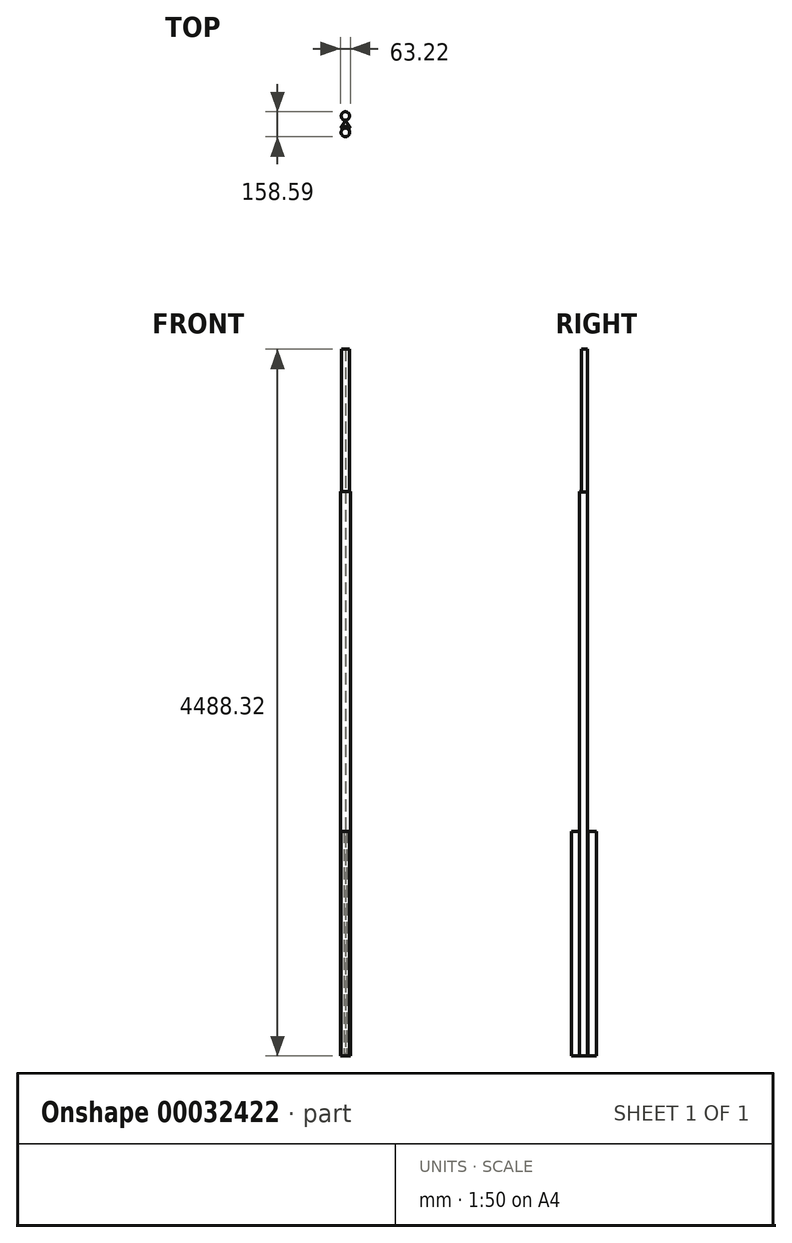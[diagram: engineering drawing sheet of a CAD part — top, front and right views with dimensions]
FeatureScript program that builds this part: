
annotation { "Feature Type Name" : "Feature", "Feature Type Description" : "" }
export const myFeature = defineFeature(function(context is Context, id is Id, definition is map)
    precondition{}
    {
        {
            var Q0;
            Q0=qCreatedBy(makeId("Top.planeOp"),FACE);
            var sketch = newSketch(context, id + "F0", { "sketchPlane" : qUnion([Q0])});
            skLineSegment(sketch, "E0", {"start": v(0, 51.9) * mm, "end": v(0, -26.05) * mm});
            skSolve(sketch);
        }
        {
            var Q0;
            Q0=qCreatedBy(makeId("Top.planeOp"),FACE);
            var sketch = newSketch(context, id + "F1", { "sketchPlane" : qUnion([Q0])});
            skLineSegment(sketch, "E1", {"start": v(0, 38.05) * mm, "end": v(-31.61, -10.02) * mm});
            skLineSegment(sketch, "E2", {"start": v(-31.61, -10.02) * mm, "end": v(0, -10.02) * mm});
            skLineSegment(sketch, "E3.MirrorCS", {"start": v(0, 38.05) * mm, "end": v(31.61, -10.02) * mm});
            skLineSegment(sketch, "E4.MirrorCS", {"start": v(31.61, -10.02) * mm, "end": v(0, -10.02) * mm});
            skSolve(sketch);
        }
        {
            var Q0;
            Q0=makeQuery(id+"F1.imprint","IMPRINT",FACE,{"disambiguationData":[TD([[makeQuery(id+"F1.imprint","IMPRINT",EDGE,{"derivedFrom":sQuery(id+"F1.wireOp",EDGE,"E1")}),1.0]])]});
            extrude(context, id + "F2", {"entities" : qUnion([Q0]), "depth" : 3583.24 * mm});
        }
        {
            var Q0;
            Q0=qCreatedBy(makeId("Top.planeOp"),FACE);
            var sketch = newSketch(context, id + "F3", { "sketchPlane" : qUnion([Q0])});
            skLineSegment(sketch, "E5", {"start": v(0, 38.05) * mm, "end": v(25.12, 0) * mm});
            skLineSegment(sketch, "E6", {"start": v(25.12, 0) * mm, "end": v(-25.55, 0) * mm});
            skLineSegment(sketch, "E7", {"start": v(-25.55, 0) * mm, "end": v(0, 38.05) * mm});
            skSolve(sketch);
        }
        {
            var Q0;
            Q0 = qSketchRegion(id + "F3", true);
            extrude(context, id + "F4", {"entities" : qUnion([Q0]), "depth" : 4488.32 * mm, "hasSecondDirection" : true, "secondDirectionOppositeDirection" : false, "secondDirectionDepth" : 3580.85 * mm});
        }
        {
            var Q0;
            Q0=qCreatedBy(makeId("Top.planeOp"),FACE);
            var sketch = newSketch(context, id + "F5", { "sketchPlane" : qUnion([Q0])});
            skCircle(sketch, "E8", {"center": v(0, -36.2) * mm, "radius": 27.25 * mm});
            skCircle(sketch, "E9", {"center": v(0, 68.54) * mm, "radius": 26.6 * mm});
            skSolve(sketch);
        }
        {
            var Q0;
            Q0=makeQuery(id+"F5.imprint","IMPRINT",FACE,{"disambiguationData":[TD([[makeQuery(id+"F5.imprint","IMPRINT",EDGE,{"derivedFrom":sQuery(id+"F5.wireOp",EDGE,"E8")}),1.0]])]});
            var Q1;
            Q1=makeQuery(id+"F5.imprint","IMPRINT",FACE,{"disambiguationData":[TD([[makeQuery(id+"F5.imprint","IMPRINT",EDGE,{"derivedFrom":sQuery(id+"F5.wireOp",EDGE,"E9")}),1.0]])]});
            extrude(context, id + "F6", {"entities" : qUnion([Q0, Q1]), "operationType" : NewBodyOperationType.ADD, "depth" : 1426.9 * mm});
        }
    });
